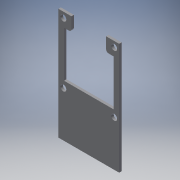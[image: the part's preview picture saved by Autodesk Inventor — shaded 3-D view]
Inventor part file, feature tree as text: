
AUTODESK INVENTOR PART (.ipt)
format: ipt  version: 2018 (Build 220112000, 112)  size: 151,552 bytes
history: native  units: mm
features: sketch x4, projected_geometry x3, extrude x2, hole x2, fillet x1
ambient origin geometry x8: Origin, YZ Plane, XZ Plane, XY Plane, X Axis, Y Axis, Z Axis, Center Point
bodies: Solid1 (feature_tree)
feature tree (12):
  extrude  "Extrusion1"  Depth=45.0mm
  extrude  "Extrusion2"  Depth=2.25mm
  hole  "Hole1"  [1 undecoded]
  hole  "Hole2"  [1 undecoded]
  fillet  "Fillet1"  Radius=14.0mm
  sketch  "Sketch1"  dims[d0=24.5mm d1=45.0mm]
  sketch  "Sketch2"  dims[d2=1.0mm d3=0.0mm d4=2.25mm]
  projected_geometry  "Projected Loop1"
  sketch  "Sketch3"  dims[d5=20.0mm d6=2.25mm]
  projected_geometry  "Projected Loop2"
  sketch  "Sketch4"  dims[d7=5.25mm d8=5.25mm d9=14.0mm d10=5.25mm d11=18.5mm d12=10.0mm d13=0.0mm d14=20.5mm d15=2.0mm d16=2.195mm d17=2.0mm d18=2.4mm d19=6.0mm d20=4.4mm d21=2.0mm d22=90.0deg d23=8.0mm d24=20.594885mm d25=20.5mm d26=26.65mm d27=2.0mm d28=2.0mm d29=2.4mm d30=6.0mm d31=4.4mm d32=2.0mm d33=90.0deg d34=8.0mm d35=20.594885mm d36=0.5mm]
  projected_geometry  "Projected Loop3"
note: 2 required parameter values undecoded (feature->parameter linkage not recoverable at this tier; creation-order binding heuristic only, values carry confidence <= 0.55)
